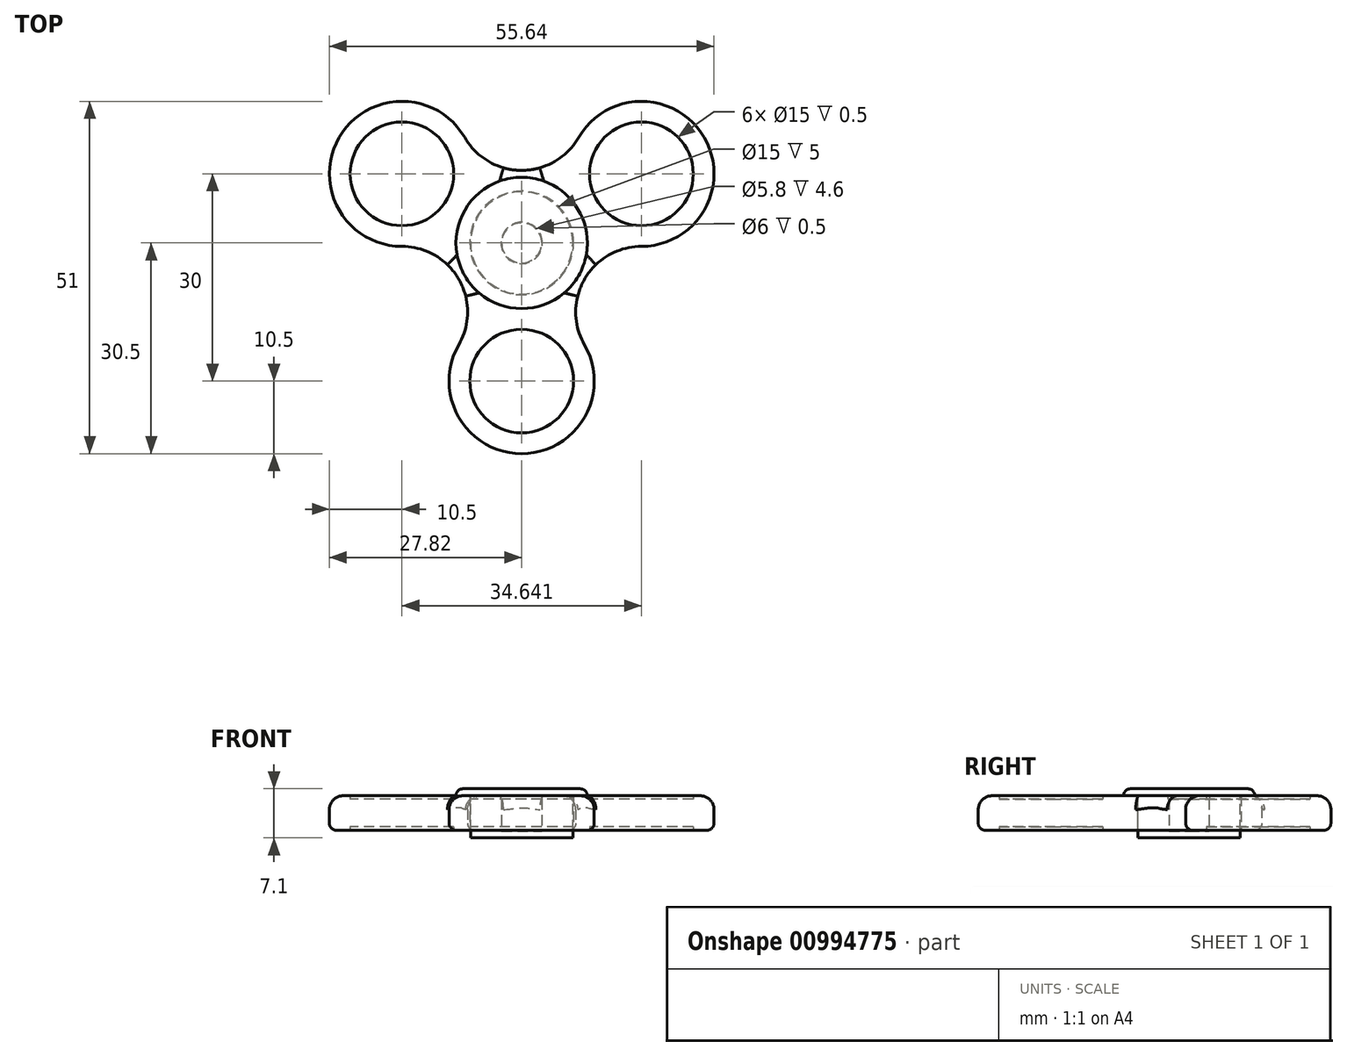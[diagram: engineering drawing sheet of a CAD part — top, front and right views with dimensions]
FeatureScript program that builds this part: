
annotation { "Feature Type Name" : "Feature", "Feature Type Description" : "" }
export const myFeature = defineFeature(function(context is Context, id is Id, definition is map)
    precondition{}
    {
        {
            var Q0;
            Q0=qCreatedBy(makeId("Top.planeOp"),FACE);
            var sketch = newSketch(context, id + "F0", { "sketchPlane" : qUnion([Q0])});
            skCircle(sketch, "E0", {"center": v(0, 0) * mm, "radius": 7.5 * mm});
            skCircle(sketch, "E1", {"center": v(0, -20) * mm, "radius": 7.5 * mm});
            skArc(sketch, "E2", {"start": v(-9.1, -14.75) * mm, "mid": v(0, -30.5) * mm, "end": v(9.1, -14.75) * mm});
            skArc(sketch, "E3.1.0", {"start": v(17.32, -0.5) * mm, "mid": v(26.41, 15.25) * mm, "end": v(8.23, 15.25) * mm});
            skCircle(sketch, "E3.1.1", {"center": v(17.32, 10) * mm, "radius": 7.5 * mm});
            skArc(sketch, "E3.2.0", {"start": v(-8.23, 15.25) * mm, "mid": v(-26.41, 15.25) * mm, "end": v(-17.32, -0.5) * mm});
            skCircle(sketch, "E3.2.1", {"center": v(-17.32, 10) * mm, "radius": 7.5 * mm});
            skArc(sketch, "E4", {"start": v(-9.1, -14.75) * mm, "mid": v(-9.1, -5.25) * mm, "end": v(-17.32, -0.5) * mm});
            skArc(sketch, "E5.1.0", {"start": v(17.32, -0.5) * mm, "mid": v(9.1, -5.25) * mm, "end": v(9.1, -14.75) * mm});
            skArc(sketch, "E5.2.0", {"start": v(-8.23, 15.25) * mm, "mid": v(0, 10.5) * mm, "end": v(8.23, 15.25) * mm});
            skSolve(sketch);
        }
        {
            var Q0;
            Q0 = qSketchRegion(id + "F0", true);
            extrude(context, id + "F1", {"entities" : qUnion([Q0]), "endBound" : BoundingType.SYMMETRIC, "depth" : 5 * mm, "offsetDistance" : 25 * mm});
        }
        {
            var Q0;
            Q0=makeQuery(id+"F0.imprint","IMPRINT",FACE,{"disambiguationData":[TD([[makeQuery(id+"F0.imprint","IMPRINT",EDGE,{"derivedFrom":sQuery(id+"F0.wireOp",EDGE,"E1")}),1.0]])]});
            var Q1;
            Q1=makeQuery(id+"F0.imprint","IMPRINT",FACE,{"disambiguationData":[TD([[makeQuery(id+"F0.imprint","IMPRINT",EDGE,{"derivedFrom":sQuery(id+"F0.wireOp",EDGE,"E3.1.1")}),1.0]])]});
            var Q2;
            Q2=makeQuery(id+"F0.imprint","IMPRINT",FACE,{"disambiguationData":[TD([[makeQuery(id+"F0.imprint","IMPRINT",EDGE,{"derivedFrom":sQuery(id+"F0.wireOp",EDGE,"E3.2.1")}),1.0]])]});
            extrude(context, id + "F2", {"entities" : qUnion([Q0, Q1, Q2]), "operationType" : NewBodyOperationType.ADD, "endBound" : BoundingType.SYMMETRIC, "depth" : 4 * mm, "offsetDistance" : 25 * mm});
        }
        {
            var Q0;
            Q0=makeQuery(id+"F1.opExtrude","CAP_FACE",FACE,{"disambiguationData":[OSD([sQuery(id+"F0.wireOp",EDGE,"E0"),sQuery(id+"F0.wireOp",EDGE,"E1"),sQuery(id+"F0.wireOp",EDGE,"E2"),sQuery(id+"F0.wireOp",EDGE,"E3.1.0"),sQuery(id+"F0.wireOp",EDGE,"E3.1.1"),sQuery(id+"F0.wireOp",EDGE,"E3.2.0"),sQuery(id+"F0.wireOp",EDGE,"E3.2.1"),sQuery(id+"F0.wireOp",EDGE,"E4"),sQuery(id+"F0.wireOp",EDGE,"E5.1.0"),sQuery(id+"F0.wireOp",EDGE,"E5.2.0")])],"isStart":false});
            var sketch = newSketch(context, id + "F3", { "sketchPlane" : qUnion([Q0])});
            skCircle(sketch, "E6.0", {"center": v(0, 0) * mm, "radius": 9.5 * mm});
            skCircle(sketch, "E7.0", {"center": v(0, 0) * mm, "radius": 7.4 * mm});
            skCircle(sketch, "E8", {"center": v(0, 0) * mm, "radius": 3 * mm});
            skSolve(sketch);
        }
        {
            var Q0;
            Q0=makeQuery(id+"F3.imprint","IMPRINT",FACE,{"disambiguationData":[TD([[makeQuery(id+"F3.imprint","IMPRINT",EDGE,{"derivedFrom":sQuery(id+"F3.wireOp",EDGE,"E7.0")}),1.0]])]});
            extrude(context, id + "F4", {"entities" : qUnion([Q0]), "oppositeDirection" : true, "depth" : 5.1 * mm, "offsetDistance" : 25 * mm});
        }
        {
            var Q0;
            Q0 = qSketchRegion(id + "F3", true);
            var Q1;
            Q1=makeQuery(id+"F3.imprint","IMPRINT",FACE,{"disambiguationData":[TD([[makeQuery(id+"F3.imprint","IMPRINT",EDGE,{"derivedFrom":sQuery(id+"F3.wireOp",EDGE,"E7.0")}),1.0]])]});
            var Q2;
            Q2=makeQuery(id+"F3.imprint","IMPRINT",FACE,{"disambiguationData":[TD([[makeQuery(id+"F3.imprint","IMPRINT",EDGE,{"derivedFrom":sQuery(id+"F3.wireOp",EDGE,"E8")}),1.0]])]});
            extrude(context, id + "F5", {"entities" : qUnion([Q0, Q1, Q2]), "operationType" : NewBodyOperationType.ADD, "depth" : 1 * mm, "offsetDistance" : 25 * mm});
        }
        {
            var Q0;
            Q0=makeQuery(id+"F4.opExtrude","CAP_FACE",FACE,{"disambiguationData":[OSD([sQuery(id+"F3.wireOp",EDGE,"E7.0"),sQuery(id+"F3.wireOp",EDGE,"E8")])],"isStart":false});
            var sketch = newSketch(context, id + "F6", { "sketchPlane" : qUnion([Q0])});
            skCircle(sketch, "E9.0", {"center": v(0, 0) * mm, "radius": 2.9 * mm});
            skCircle(sketch, "E10.0", {"center": v(0, 0) * mm, "radius": 9.5 * mm});
            skSolve(sketch);
        }
        {
            var Q0;
            Q0=makeQuery(id+"F6.imprint","IMPRINT",FACE,{"disambiguationData":[TD([[makeQuery(id+"F6.imprint","IMPRINT",EDGE,{"derivedFrom":sQuery(id+"F6.wireOp",EDGE,"E9.0")}),-1.0]])]});
            var Q1;
            Q1=makeQuery(id+"F2.opExtrude","CAP_FACE",FACE,{"disambiguationData":[OSD([sQuery(id+"F0.wireOp",EDGE,"E3.2.1")])],"isStart":false});
            extrude(context, id + "F7", {"entities" : qUnion([Q0]), "endBound" : BoundingType.UP_TO_SURFACE, "oppositeDirection" : true, "depth" : 1 * mm, "endBoundEntityFace" : qUnion([Q1]), "offsetDistance" : 25 * mm});
        }
        {
            var Q0;
            Q0=makeQuery(id+"F6.imprint","IMPRINT",FACE,{"disambiguationData":[TD([[makeQuery(id+"F6.imprint","IMPRINT",EDGE,{"derivedFrom":sQuery(id+"F6.wireOp",EDGE,"E10.0")}),-1.0]])]});
            var Q1;
            Q1=makeQuery(id+"F6.imprint","IMPRINT",FACE,{"disambiguationData":[TD([[makeQuery(id+"F6.imprint","IMPRINT",EDGE,{"derivedFrom":makeQuery(id+"F4.opExtrude","CAP_EDGE",EDGE,{"disambiguationData":[OSD([sQuery(id+"F3.wireOp",EDGE,"E7.0")])],"isStart":false})}),-1.0]])]});
            var Q2;
            Q2=makeQuery(id+"F6.imprint","IMPRINT",FACE,{"disambiguationData":[TD([[makeQuery(id+"F6.imprint","IMPRINT",EDGE,{"derivedFrom":sQuery(id+"F6.wireOp",EDGE,"E9.0")}),1.0]])]});
            var Q3;
            Q3=makeQuery(id+"F6.imprint","IMPRINT",FACE,{"disambiguationData":[TD([[makeQuery(id+"F6.imprint","IMPRINT",EDGE,{"derivedFrom":sQuery(id+"F6.wireOp",EDGE,"E9.0")}),-1.0]])]});
            var Q4;
            Q4=sQuery(id+"F6.wireOp",EDGE,"E10.0");
            extrude(context, id + "F8", {"entities" : qUnion([Q0, Q1, Q2, Q3]), "operationType" : NewBodyOperationType.ADD, "surfaceEntities" : qUnion([Q4]), "depth" : 1 * mm, "offsetDistance" : 25 * mm});
        }
        {
            var Q0;
            Q0=makeQuery(id+"F1.opExtrude","CAP_EDGE",EDGE,{"disambiguationData":[OSD([sQuery(id+"F0.wireOp",EDGE,"E3.2.0")])],"isStart":false});
            fillet(context, id + "F9", {"entities" : qUnion([Q0]), "radius" : 2 * mm, "tangentPropagation" : true, "allowEdgeOverflow" : false});
        }
        {
            var Q0;
            Q0=makeQuery(id+"F5.opExtrude","CAP_EDGE",EDGE,{"disambiguationData":[OSD([sQuery(id+"F3.wireOp",EDGE,"E6.0")])],"isStart":false});
            fillet(context, id + "F10", {"entities" : qUnion([Q0]), "radius" : 1 * mm, "tangentPropagation" : true, "allowEdgeOverflow" : false});
        }
        {
            var Q0;
            Q0=makeQuery(id+"F1.opExtrude","CAP_EDGE",EDGE,{"disambiguationData":[OSD([sQuery(id+"F0.wireOp",EDGE,"E3.2.0")])],"isStart":true});
            var Q1;
            Q1=makeQuery(id+"F8.opExtrude","CAP_EDGE",EDGE,{"disambiguationData":[OSD([sQuery(id+"F6.wireOp",EDGE,"E10.0")])],"isStart":false});
            fillet(context, id + "F11", {"entities" : qUnion([Q0, Q1]), "radius" : 1 * mm, "tangentPropagation" : true, "allowEdgeOverflow" : false});
        }
    });
